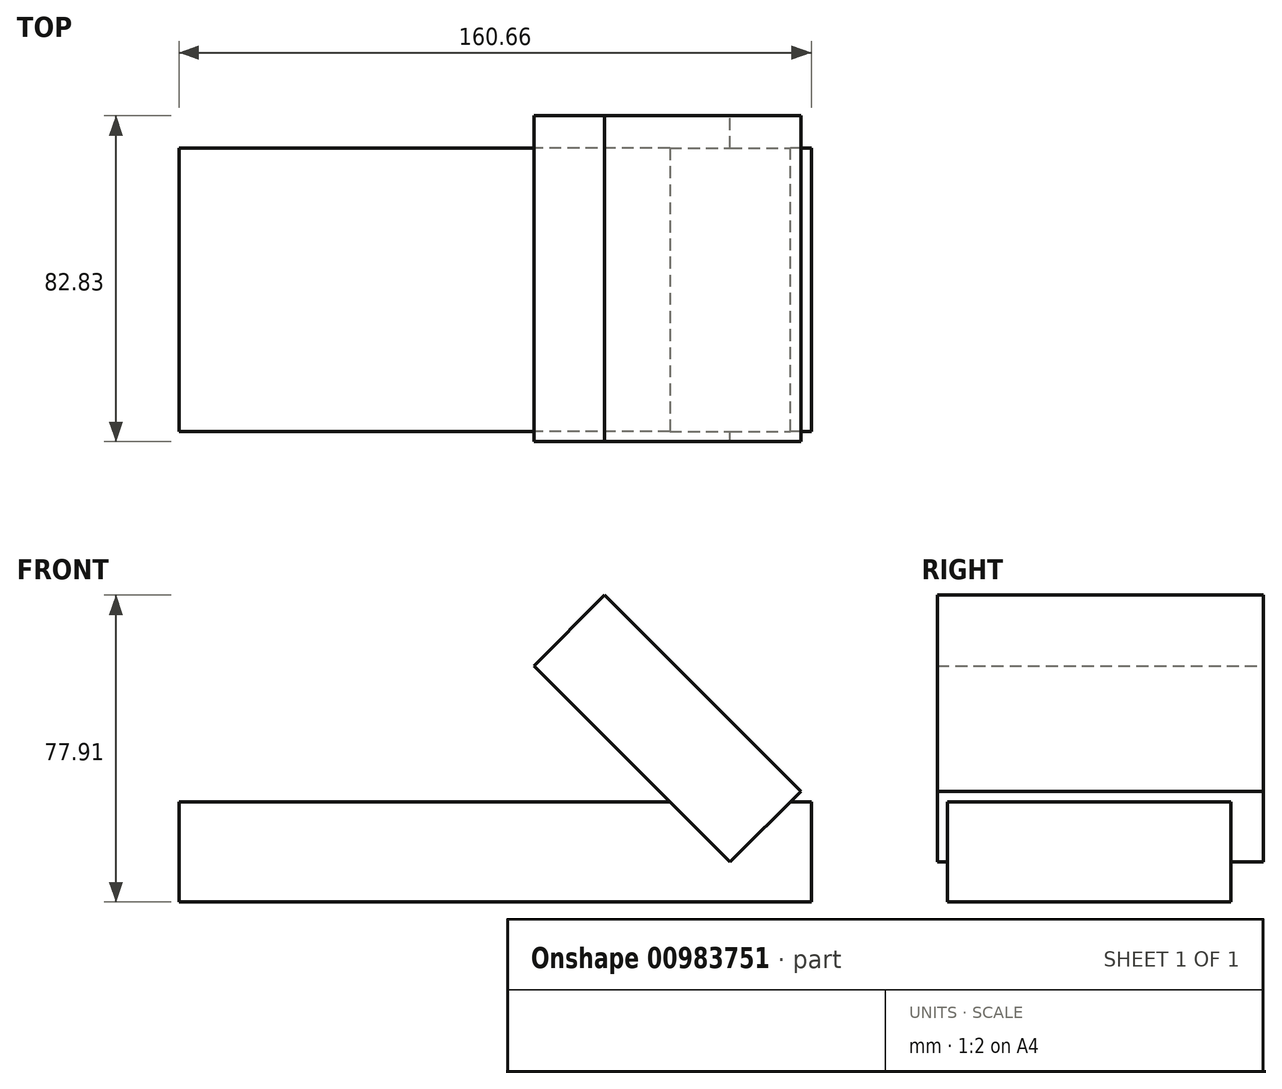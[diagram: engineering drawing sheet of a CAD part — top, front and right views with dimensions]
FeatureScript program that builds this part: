
annotation { "Feature Type Name" : "Feature", "Feature Type Description" : "" }
export const myFeature = defineFeature(function(context is Context, id is Id, definition is map)
    precondition{}
    {
        {
            var Q0;
            Q0=qCreatedBy(makeId("Top.planeOp"),FACE);
            var sketch = newSketch(context, id + "F0", { "sketchPlane" : qUnion([Q0])});
            skLineSegment(sketch, "E0.bottom", {"start": v(80.33, -35.98) * mm, "end": v(-80.33, -35.98) * mm});
            skLineSegment(sketch, "E0.top", {"start": v(80.33, 35.98) * mm, "end": v(-80.33, 35.98) * mm});
            skLineSegment(sketch, "E0.left", {"start": v(80.33, -35.98) * mm, "end": v(80.33, 35.98) * mm});
            skLineSegment(sketch, "E0.right", {"start": v(-80.33, -35.98) * mm, "end": v(-80.33, 35.98) * mm});
            skPoint(sketch, "E0.middle", {"position": v(0, 0) * mm});
            skSolve(sketch);
        }
        {
            var Q0;
            Q0 = qSketchRegion(id + "F0", true);
            extrude(context, id + "F1", {"entities" : qUnion([Q0]), "depth" : 25.4 * mm, "offsetDistance" : 25.4 * mm});
        }
        {
            var Q0;
            Q0=makeQuery(id+"F1.opExtrude","CAP_EDGE",EDGE,{"disambiguationData":[OSD([sQuery(id+"F0.wireOp",EDGE,"E0.left")])],"isStart":false});
            var Q1;
            Q1=makeQuery(id+"F1.opExtrude","CAP_FACE",FACE,{"disambiguationData":[OSD([sQuery(id+"F0.wireOp",EDGE,"E0.bottom"),sQuery(id+"F0.wireOp",EDGE,"E0.top"),sQuery(id+"F0.wireOp",EDGE,"E0.left"),sQuery(id+"F0.wireOp",EDGE,"E0.right")])],"isStart":false});
            cPlane(context, id + "F2", {"entities" : qUnion([Q0, Q1]), "cplaneType" : CPlaneType.LINE_ANGLE, "offset" : 25.4 * mm, "angle" : 45 * degree, "width" : 152.4 * mm, "height" : 152.4 * mm});
        }
        {
            var Q0;
            Q0=qCreatedBy(id+"F2.planeOp",FACE);
            var sketch = newSketch(context, id + "F3", { "sketchPlane" : qUnion([Q0])});
            skLineSegment(sketch, "E1.bottom", {"start": v(38.6, 35.42) * mm, "end": v(-44.22, 35.42) * mm});
            skLineSegment(sketch, "E1.top", {"start": v(38.6, -35.08) * mm, "end": v(-44.22, -35.08) * mm});
            skLineSegment(sketch, "E1.left", {"start": v(38.6, 35.42) * mm, "end": v(38.6, -35.08) * mm});
            skLineSegment(sketch, "E1.right", {"start": v(-44.22, 35.42) * mm, "end": v(-44.22, -35.08) * mm});
            skSolve(sketch);
        }
        {
            var Q0;
            Q0 = qSketchRegion(id + "F3", true);
            extrude(context, id + "F4", {"entities" : qUnion([Q0]), "operationType" : NewBodyOperationType.ADD, "depth" : 25.4 * mm, "offsetDistance" : 25.4 * mm});
        }
    });
